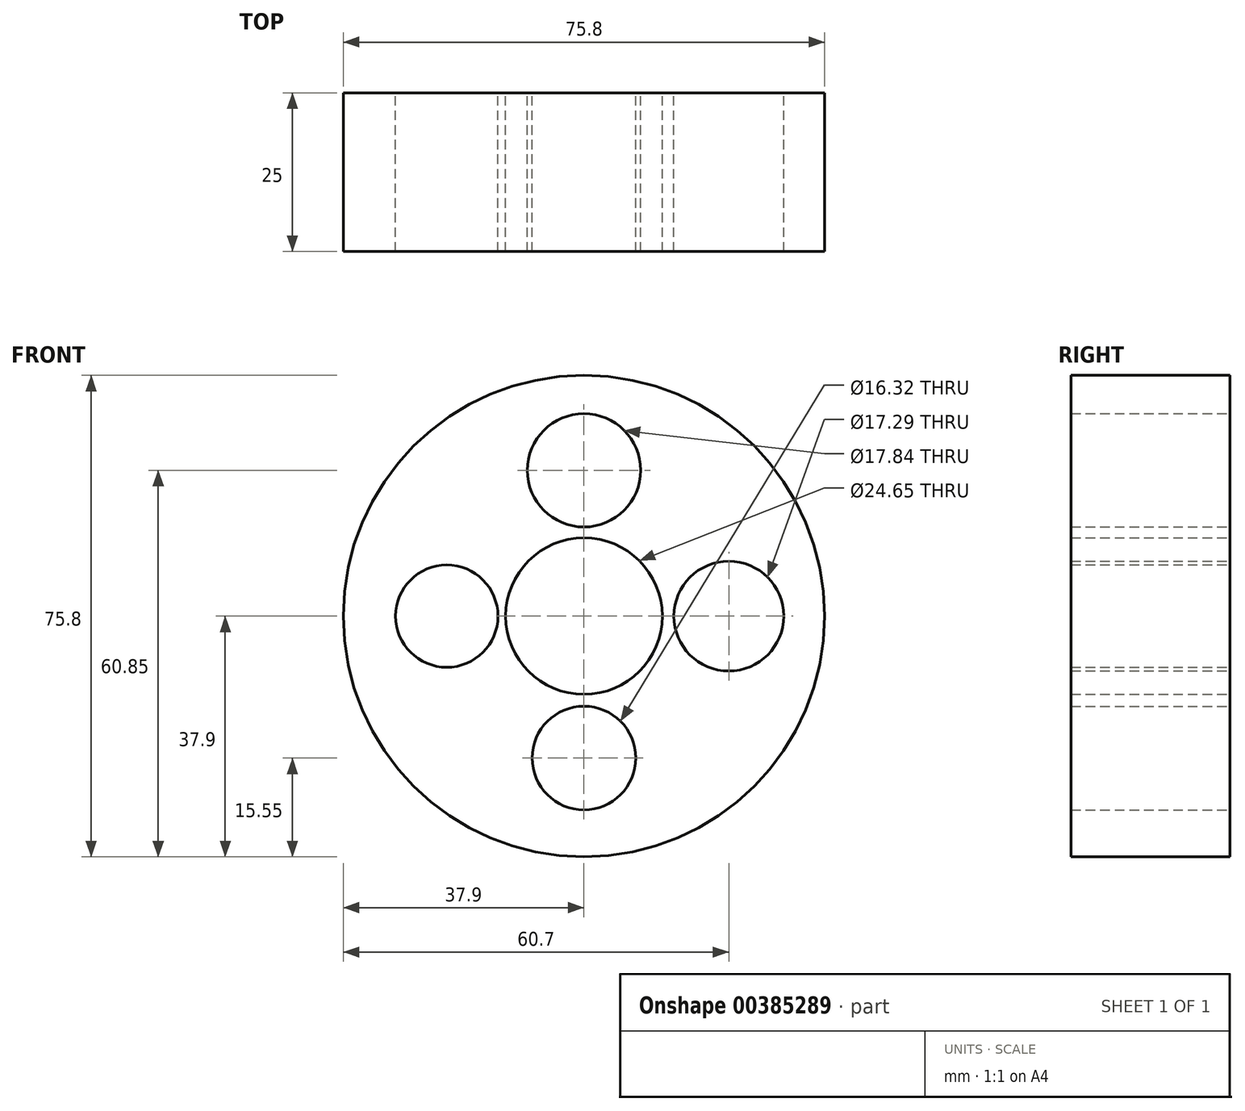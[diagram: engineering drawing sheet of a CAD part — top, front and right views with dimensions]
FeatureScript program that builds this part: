
annotation { "Feature Type Name" : "Feature", "Feature Type Description" : "" }
export const myFeature = defineFeature(function(context is Context, id is Id, definition is map)
    precondition{}
    {
        {
            var Q0;
            Q0=qCreatedBy(makeId("Front.planeOp"),FACE);
            var sketch = newSketch(context, id + "F0", { "sketchPlane" : qUnion([Q0])});
            skCircle(sketch, "E0", {"center": v(0, 0) * mm, "radius": 37.9 * mm});
            skCircle(sketch, "E1", {"center": v(0, 0) * mm, "radius": 34.35 * mm});
            skCircle(sketch, "E2", {"center": v(0, 0) * mm, "radius": 12.32 * mm});
            skCircle(sketch, "E3", {"center": v(0, 0) * mm, "radius": 9.24 * mm});
            skCircle(sketch, "E4", {"center": v(0, -22.35) * mm, "radius": 8.16 * mm});
            skCircle(sketch, "E5", {"center": v(22.8, 0) * mm, "radius": 8.64 * mm});
            skCircle(sketch, "E6", {"center": v(-21.6, 0) * mm, "radius": 8.06 * mm});
            skCircle(sketch, "E7", {"center": v(0, 22.95) * mm, "radius": 8.92 * mm});
            skSolve(sketch);
        }
        {
            var Q0;
            Q0 = qSketchRegion(id + "F0", true);
            var Q1;
            Q1=makeQuery(id+"F0.imprint","IMPRINT",FACE,{"disambiguationData":[TD([[makeQuery(id+"F0.imprint","IMPRINT",EDGE,{"derivedFrom":sQuery(id+"F0.wireOp",EDGE,"E1")}),1.0]])]});
            extrude(context, id + "F1", {"entities" : qUnion([Q0, Q1]), "depth" : 25 * mm});
        }
    });
